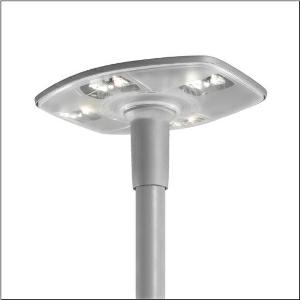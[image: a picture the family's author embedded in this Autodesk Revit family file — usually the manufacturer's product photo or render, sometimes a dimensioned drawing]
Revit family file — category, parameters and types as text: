
# Revit family: dl_r__30_led___st1_2c_5xa513281b08a5_eae4
name_source: partatom
category: Lighting Fixtures
units: mm (PartAtom-declared; Revit-internal decimal feet)

## family parameters
Cut with Voids When Loaded = No
Host = Face
Light Source = No
Part Type = Normal
Room Calculation Point = No
Round Connector Dimension = Use Diameter
Shared = No

## types (1)
- --- (1 x LED, 4590 lm, 49 W, 3000K)
    Apparent Load = 49 VA
    CIE Flux Codes = 32 71 98 100 100
    Color Rendering = 80
    Color Temperature = 3000K
    Default Elevation = 1800 mm
    Description = DL® 30 LED, mast luminaire, primary light control with 3 zone facetted reflector, of plastic, aluminium vaporised, highly specular, primary optical cover: cover, of PMMA, structured, transparent, light distribution: ST1.2c, light emission: direct distribution, primary light characteristic: asymmetric, crossroads, installation type: post-top, LED, High Power LED, rated luminous flux: 4.590lm, luminous efficacy: 94lm/W, light colour: 830, colour temperature: 3000K, control gear: ECG Plus, control: flexible luminous flux parameterisation, time-dependent luminous flux control, constant luminous flux control, digital communication interface, power reduction, electronic power reduction, mains connection: 230..240V, AC, 50/60Hz, start of lifetime: 49W, end of service life: 51W, reduction: 22W, luminaire housing, of diecast aluminium, powder-coated, Siteco® metallic grey (DB 702S), length: 600mm, width: 510mm, height: 290mm, spigot size: d x l = 76 x 100mm (post-top) | with reducer (optional accessory) 60 x 100mm, protection rating (complete): IP66, insulation class (complete): insulation class II (safety insulation), certification: CE, ENEC, VDE, impact resistance: IK08, permissible operating ambient temperature: -25..+30°C, standard-compliant lighting for roads and squares, packaging unit: 1 piece

Light Distribution: ST1.2c
    Height = 290 mm
    Lamp = 1 x LED
    Lamp Light Flux = 4590 lm
    Lamp Power = 49 W
    Lamp count = 1
    Length = 510 mm
    Luminous efficacy = 94 lm/W
    Manufacturer = Siteco
    ModVariant = No
    Model = 5XA513281B08A5
    Number of Poles = 1
    OnlyDefault = Yes
    Power Factor = 1
    Product Name = DL® 30 LED | ST1.2c
    Product group = mast luminaire | pylon top
    ProductGroupID = 6100
    Protection Class = Protection class II
    Protection Degree = IP 66
    RLX_Detail_Level = 1
    RLX_Emergency_Light_Flux = 0 lm
    RLX_Emergency_Type = 0
    RLX_Emergency_Type_DB = No
    RlxData = <blob elided: 86569 chars, md5=7776634a>
    Socket = socket
    Standby Power = 0 W
    System Light Flux = 4590 lm
    System Power = 49 W
    Type Comments = factory setting: luminous flux: 100 % | dim-lin: 254 | 497 mA
    Type Image = l_1006003.jpg
    URL = http://relux.com
    VarID = @adj_137791
    Voltage = 0 V
    Weight = 0.00 kg
    Width = 600 mm

## geometry (parser evidence)
native form markers: Blend x4, Sweep x11
no freeform markers — native parametric forms only
